# Revit family: QF_ELECTROLUXPROFESSIONAL_1LSN0H_TD6-7_E
name_source: partatom
category: Attrezzature speciali
units: mm (PartAtom-declared; Revit-internal decimal feet)

## family parameters
Basato su piano di lavoro = No
Condiviso = No
Punto di calcolo locali = No
Quota connettore circolare = Usa diametro
Sempre verticale = Sì
Taglio con vuoti quando caricato = No
Tipo di parte = Normale

## types (74) — shared parameters
Depth Actual = 845 mm  [stored 2.77231 ft]
Height Actual = 1050 mm
Latent Heat Output = 0.0
Length Actual = 600 mm  [stored 1.9685 ft]
Modello = TD6-7
Produttore = Electrolux Professional
Sensible Heat Output = 0.0
URL = www.electroluxprofessional.com
Weight = 109
zero-valued in all types: Gas KW, Prospetto di default, Steam Pounds per Hour

## per-type parameters (varying)
| type | Cycle | Descrizione | Item Number | Phase | Volts | Watts |
| 9871830026 | 60 Hz | TUMBLE DRYER TD6-7 MARINE 7KG GALVA.DRUM EL 6KW 230/60/3 COMPASS PRO 6G82 SE SILVER DO.LEFT DISCON. | 1L0EHY | 3 | 230 V | 6300 W |
| 9871830016 | 50 Hz | TUMBLE DRYER TD6-7 7KG SST DRUM EL 6KW 400/50/3N COMPASS PRO 6L80 EU SILVER DO.LEFT EXT.PM. DISCON. 2.I/O | 1L0EGP | 3 | 400 V | 6300 W |
| 9871830160 | 60 Hz | TUMBLE DRYER TD6-7 7KG SST DRUM EL 6KW 200/60/3 COMPASS PRO 6G86 JP SILVER DO.LEFT DISCON. | 1L0H7K | 3 | 200 V | 6300 W |
| 9871830140 | 60 Hz | TUMBLE DRYER TD6-7 7KG GALVA.DRUM EL 6KW 208-240/60/3 COMPASS PRO 6G81 EU SILVER DO.LEFT.INS. MB DISCON. | 1LA244 | 3 | 240 V | 4800 W |
| 9871830056 | 50 Hz | TUMBLE DRYER TD6-7 MARINE 7KG GALVA.DRUM EL 3KW 220-230/50/1N COMPASS PRO 6G81 SE SILVER DO.LEFT MB DISCON. | 1LSN72 | 1 | 230 V | 3300 W |
| 9871830031 | 50 Hz | TUMBLE DRYER TD6-7 7KG GALVA.DRUM EL 6KW 400/50/3N COMPASS PRO 6G82 SE SILVER DO.LEFT | 1L0EKF | 3 | 400 V | 6300 W |
| 9871830096 | 50 Hz | TUMBLE DRYER TD6-7 MARINE 7KG GALVA.DRUM EL 6KW 230/50/3 COMPASS PRO 6G81 SE SILVER DO.LEFT MB DISCON. | 1L0EPL | 3 | 230 V | 6300 W |
| 9871830086 | 60 Hz | TUMBLE DRYER TD6-7 MARINE 7KG GALVA.DRUM EL 4,5KW 230/60/1 COMPASS PRO 6G82 EU SILVER DO.LEFT DISCON. | 1L0ENK | 1 | 230 V | 3300 W |
| 9871830001 | 50 Hz | TUMBLE DRYER TD6-7 7KG SST DRUM EL 6KW 400/50/3N COMPASS PRO 6A81 SE SILVER DO.LEFT.INS. MB | 1LSN1V | 3 | 400 V | 6300 W |
| 9871830011 | 50 Hz | TUMBLE DRYER TD6-7 7KG SST DRUM EL 6KW 230/50/1N COMPASS PRO 6G81 EU SILVER DO.LEFT.INS. MB DISCON. | 1LSN23 | 1 | 230 V | 3300 W |
| 9871830061 | 60 Hz | TUMBLE DRYER TD6-7 7KG GALVA.DRUM EL 4,5KW 208-240/60/1 COMPASS PRO 6L80 EU SILVER DO.LEFT DISCON. | 1L0EKU | 1 | 240 V | 3300 W |
| 9871830051 | 50 Hz | TUMBLE DRYER TD6-7 7KG GALVA.DRUM EL 6KW 400/50/3N COMPASS PRO 6G81 EU SILVER DO.LEFT.INS. ELS-NETW. PREP.CB MB DISCON. | 1L8213 | 3 | 400 V | 6300 W |
| 9871830168 | 60 Hz | TUMBLE DRYER TD6-7 MARINE 7KG SST DRUM EL 6KW 400/60/3N COMPASS PRO 6G81 EU SST/SILVER DO.LEFT PREP.CB MB DISCON. 2.I/O | 1LM0CB | 3 | 400 V | 6300 W |
| 9871830039 | 50 Hz | TUMBLE DRYER TD6-7 7KG SST DRUM EL 6KW 400/50/3N COMPASS PRO 6L80 EU SST/SILVER DO.LEFT EXT.PM. DISCON. 2.I/O | 1L80HG | 3 | 400 V | 6300 W |
| 9871830029 | 50 Hz | TUMBLE DRYER TD6-7 7KG SST DRUM EL 3KW 220-230/50/1N COMPASS PRO 6L80 EU SST/SILVER DO.LEFT EXT.PM. DISCON. 2.I/O | 1L0EJZ | 1 | 230 V | 3300 W |
| 9871830019 | 60 Hz | TUMBLE DRYER TD6-7 MARINE 7KG SST DRUM EL 3KW 230/60/1N COMPASS PRO 6G81 EU SILVER DO.LEFT MB DISCON. | 1L0EGT | 1 | 230 V | 3300 W |
| 9871830105 | 50 Hz | TUMBLE DRYER TD6-7 MARINE 7KG GALVA.DRUM EL 4,5KW 400/50/3 COMPASS PRO 6G81 SE SILVER DO.LEFT MB DISCON. | 1L0FUW | 3 | 400 V | 4800 W |
| 9871830079 | 60 Hz | TUMBLE DRYER TD6-7 MARINE 7KG GALVA.DRUM EL 6KW 400/60/3N COMPASS PRO 6G81 SE SILVER DO.LEFT MB DISCON. | 1L0ELT | 3 | 400 V | 6300 W |
| 9871830059 | 50 Hz | TUMBLE DRYER TD6-7 7KG GALVA.DRUM EL 6KW 400/50/3N COMPASS PRO 6G81 EU SILVER DO.LEFT MB DISCON. | 1L0EKK | 3 | 400 V | 6300 W |
| 9871830115 | 60 Hz | TUMBLE DRYER TD6-7 7KG GALVA.DRUM EL 6KW 400/60/3N COMPASS PRO 6G81 EU SILVER DO.LEFT MB DISCON. | 1LSNUM | 3 | 400 V | 6300 W |
| 9871830125 | 50 Hz | TUMBLE DRYER TD6-7 7KG SST DRUM EL 3KW 240/50/1N COMPASS PRO 6G81 EU SILVER DO.LEFT MB DISCON. | 1LSP7Z | 1 | 240 V | 3300 W |
| 9871830034 | 50 Hz | TUMBLE DRYER TD6-7 7KG GALVA.DRUM EL 3KW 240/50/1N COMPASS PRO 6G82 EU SILVER DO.LEFT DISCON. | 1L80HR | 1 | 240 V | 3300 W |
| 9871830014 | 50 Hz | TUMBLE DRYER TD6-7 7KG SST DRUM EL 6KW 230/50/1N COMPASS PRO 6G81 EU SILVER DO.LEFT MB DISCON. | 1L0EGM | 1 | 230 V | 6300 W |
| 9871830089 | 60 Hz | TUMBLE DRYER TD6-7 MARINE 7KG GALVA.DRUM EL 6KW 480/60/3 COMPASS PRO 6G81 SE SILVER DO.LEFT MB DISCON. | 1LSNDV | 3 | 480 V | 6300 W |
| 9871830064 | 60 Hz | TUMBLE DRYER TD6-7 MARINE 7KG SST DRUM EL 3KW 230/60/1 COMPASS PRO 6G81 EU SILVER DO.LEFT MB DISCON. | 1LSN83 | 1 | 230 V | 3300 W |
| 9871830044 | 50 Hz | TUMBLE DRYER TD6-7 7KG SST DRUM EL 6KW 415/50/3 COMPASS PRO 6G81 EU SILVER DO.LEFT MB DISCON. | 1LSN4P | 3 | 415 V | 6300 W |
| 9871830084 | 50 Hz | TUMBLE DRYER TD6-7 7KG GALVA.DRUM EL 6KW 400/50/3N COMPASS PRO 6G81 EU SILVER DO.LEFT PREP.CB MB DISCON. 2.I/O | 1LSNB2 | 3 | 400 V | 6300 W |
| 9871830126 | 50 Hz | TUMBLE DRYER TD6-7 7KG SST DRUM EL 6KW 400/50/3N COMPASS PRO 6G81 EU SILVER DO.LEFT MB DISCON. | 1L0GAN | 3 | 400 V | 6300 W |
| 9871830116 | 60 Hz | TUMBLE DRYER TD6-7 7KG GALVA.DRUM EL 6KW 400/60/3N COMPASS PRO 6G82 EU SILVER DO.LEFT DISCON. | 1LSNUN | 3 | 400 V | 6300 W |
| 9871830106 | 60 Hz | TUMBLE DRYER TD6-7 MARINE 7KG SST DRUM EL 3KW 208-240/60/1 COMPASS PRO 6L80 EU SILVER DO.LEFT EXT.PM. DISCON. 2.I/O | 1LSNHX | 1 | 240 V | 3300 W |
| 9871830176 | 50 Hz | TUMBLE DRYER TD6-7 7KG SST DRUM EL 6KW 400/50/3N COMPASS PRO 6G82 EU SILVER DO.LEFT.INS. DISCON. | 1LT6US | 3 | 400 V | 6300 W |
| 9871830173 | 50 Hz | TUMBLE DRYER TD6-7 MARINE 7KG GALVA.DRUM EL 4,5KW 230/50/1 COMPASS PRO 6G81 EU SILVER DO.LEFT MB DISCON. | 1LT6UD | 1 | 230 V | 4800 W |
| 9871830067 | 50 Hz | TUMBLE DRYER TD6-7 MARINE 7KG SST DRUM EL 6KW 400/50/3 COMPASS PRO 6G81 EU SILVER DO.LEFT MB DISCON. | 1L0ELR | 3 | 400 V | 4800 W |
| 9871830057 | 50 Hz | TUMBLE DRYER TD6-7 MARINE 7KG GALVA.DRUM EL 6KW 400/50/3 COMPASS PRO 6G81 SE SILVER DO.LEFT MB DISCON. | 1LSN73 | 3 | 400 V | 4800 W |
| 9871830047 | 60 Hz | TUMBLE DRYER TD6-7 MARINE 7KG GALVA.DRUM EL 6KW 440/60/3 COMPASS PRO 6G82 EU SST/SILVER DO.LEFT DISCON. | 1L0EKH | 3 | 440 V | 6300 W |
| 9871830153 | 60 Hz | TUMBLE DRYER TD6-7 MARINE 7KG SST DRUM EL 4,5KW 400/60/3N COMPASS PRO 6G81 SE SST/SILVER DO.LEFT MB DISCON. | 1LSPRS | 3 | 400 V | 4800 W |
| 9871830032 | 50 Hz | TUMBLE DRYER TD6-7 7KG GALVA.DRUM EL 6KW 400/50/3N COMPASS PRO 6L80 EU SILVER DO.LEFT EXT.PM. DISCON. 2.I/O | 1L80HE | 3 | 400 V | 6300 W |
| 9871830097 | 50 Hz | TUMBLE DRYER TD6-7 7KG GALVA.DRUM EL 3KW 240/50/1N COMPASS PRO 6G82 EU SILVER DO.LEFT ELS-NETW. DISCON. | 1L0ERE | 1 | 240 V | 3300 W |
| 9871830012 | 60 Hz | TUMBLE DRYER TD6-7 MARINE 7KG SST DRUM EL 6KW 440/60/3 COMPASS PRO 6G81 EU SILVER DO.LEFT.INS. MB DISCON. | 1LSN24 | 3 | 440 V | 6300 W |
| 9871830002 | 50 Hz | TUMBLE DRYER TD6-7 7KG SST DRUM EL 6KW 400/50/3N COMPASS PRO 6G81 EU SILVER DO.LEFT MB DISCON. | 1LSN0E | 3 | 400 V | 6300 W |
| 9871830087 | 60 Hz | TUMBLE DRYER TD6-7 MARINE 7KG SST DRUM EL 6KW 400/60/3N COMPASS PRO 6G81 EU SST/SILVER DO.LEFT MB DISCON. | 1LSNCS | 3 | 400 V | 6300 W |
| 9871830062 | 60 Hz | TUMBLE DRYER TD6-7 7KG GALVA.DRUM EL 4,5KW 208-240/60/3 COMPASS PRO 6L80 EU SILVER DO.LEFT DISCON. | 1L0EKV | 3 | 240 V | 4800 W |
| 9871830082 | 50 Hz | TUMBLE DRYER TD6-7 7KG SST DRUM EL 6KW 240/50/1N COMPASS PRO 6G81 EU SILVER DO.LEFT MB DISCON. | 1L0ENC | 1 | 240 V | 3300 W |
| 9871830114 | 50 Hz | TUMBLE DRYER TD6-7 7KG GALVA.DRUM EL 3KW 230/50/1N COMPASS PRO 6G82 EU SILVER DO.LEFT DISCON. | 1LSNPP | 1 | 230 V | 3300 W |
| 9871830131 | 60 Hz | TUMBLE DRYER TD6-7 MARINE 7KG GALVA.DRUM EL 6KW 400/60/3N COMPASS PRO 6L80 EU SILVER DO.LEFT EXT.PM. DISCON. 2.I/O | 1L0GEE | 3 | 400 V | 6300 W |
| 9871830035 | 60 Hz | TUMBLE DRYER TD6-7 MARINE 7KG GALVA.DRUM EL 6KW 440/60/3 COMPASS PRO 6G82 EU SILVER DO.LEFT DISCON. | 1L80HS | 3 | 440 V | 6300 W |
| 9871830111 | 60 Hz | TUMBLE DRYER TD6-7 MARINE 7KG SST DRUM EL 6KW 230/60/3 COMPASS PRO 6G81 EU SILVER DO.LEFT MB DISCON. | 1L0FYC | 3 | 230 V | 6300 W |
| 9871830015 | 60 Hz | TUMBLE DRYER TD6-7 MARINE 7KG SST DRUM EL 6KW 440/60/3 COMPASS PRO 6G81 EU SILVER DO.LEFT MB DISCON. | 1L0EGN | 3 | 440 V | 6300 W |
| 9871830121 | 50 Hz | TUMBLE DRYER TD6-7 7KG SST DRUM EL 6KW 230/50/1N COMPASS PRO 6L80 EU SILVER DO.LEFT EXT.PM. DISCON. 2.I/O | 1LA19F | 1 | 230 V | 3300 W |
| 9871830005 | 50 Hz | TUMBLE DRYER TD6-7 7KG SST DRUM EL 6KW 400/50/3N COMPASS PRO 6L80 EU SILVER DO.LEFT.INS. EXT.PM. DISCON. 2.I/O | 1LSN1Y | 3 | 400 V | 6300 W |
| 9871830065 | 60 Hz | TUMBLE DRYER TD6-7 MARINE 7KG GALVA.DRUM EL 6KW 400/60/3 COMPASS PRO 6G81 SE SILVER DO.LEFT MB DISCON. | 1LSN8F | 3 | 400 V | 6300 W |
| 9871830045 | 50 Hz | TUMBLE DRYER TD6-7 MARINE 7KG GALVA.DRUM EL 6KW 400/50/3 COMPASS PRO 6G82 EU SILVER DO.LEFT DISCON. | 1LSN4R | 3 | 400 V | 4800 W |
| 9871830030 | 50 Hz | TUMBLE DRYER TD6-7 7KG SST DRUM EL 3KW 220-230/50/1N COMPASS PRO 6L80 EU SILVER DO.LEFT EXT.PM. DISCON. 2.I/O | 1L0EK0 | 1 | 230 V | 3300 W |
| 9871830095 | 50 Hz | TUMBLE DRYER TD6-7 7KG SST DRUM EL 6KW 400/50/3 COMPASS PRO 6G81 EU SST/SILVER DO.LEFT MB DISCON. | 1L0EP5 | 3 | 400 V | 4800 W |
| 9871830129 | 50 Hz | TUMBLE DRYER TD6-7 7KG SST DRUM EL 4,5KW 220-230/50/1N COMPASS PRO 6G81 EU SILVER DO.LEFT MB DISCON. | 1L0GB8 | 1 | 230 V | 4800 W |
| 9871830139 | 50 Hz | TUMBLE DRYER TD6-7 7KG SST DRUM EL 6KW 230/50/3 COMPASS PRO 6L80 EU SILVER DO.LEFT.INS. EXT.PM. DISCON. 2.I/O | 1L0GTP | 3 | 230 V | 6300 W |
| 9871830085 | 60 Hz | TUMBLE DRYER TD6-7 7KG GALVA.DRUM EL 6KW 230/60/3 COMPASS PRO 6G82 EU SILVER DO.LEFT DISCON. | 1LSNBF | 3 | 230 V | 6300 W |
| 9871830060 | 50 Hz | TUMBLE DRYER TD6-7 7KG GALVA.DRUM EL 6KW 415/50/3N COMPASS PRO 6L80 EU SILVER DO.LEFT PREP.CB DISCON. 2.I/O | 1L821A | 3 | 415 V | 6300 W |
| 9871830159 | 50 Hz | TUMBLE DRYER TD6-7 7KG SST DRUM EL 6KW 200/50/3 COMPASS PRO 6G86 JP SILVER DO.LEFT DISCON. | 1L0H7J | 3 | 200 V | 6300 W |
| 9871830040 | 60 Hz | TUMBLE DRYER TD6-7 MARINE 7KG GALVA.DRUM EL 6KW 440/60/3 COMPASS PRO 6G82 EU SILVER DO.LEFT DISCON. | 1L80HY | 3 | 440 V | 6300 W |
| 9871830119 | 50 Hz | TUMBLE DRYER TD6-7 7KG GALVA.DRUM EL 3KW 220-230/50/1N COMPASS PRO 6G81 EU SILVER DO.LEFT MB DISCON. | 1LSNXJ | 1 | 230 V | 3300 W |
| 9871830038 | 50 Hz | TUMBLE DRYER TD6-7 7KG GALVA.DRUM EL 6KW 230/50/3 COMPASS PRO 6G81 EU SILVER DO.LEFT MB DISCON. | 1L80H4 | 3 | 230 V | 6300 W |
| 9871830102 | 60 Hz | TUMBLE DRYER TD6-7 7KG SST DRUM EL 6KW 400/60/3N COMPASS PRO 6G81 EU SST/SILVER DO.LEFT.INS. MB DISCON. | 1LSNGU | 3 | 400 V | 6300 W |
| 9871830068 | 60 Hz | TUMBLE DRYER TD6-7 7KG SST DRUM EL 6KW 440/60/3 COMPASS PRO 6G81 EU SILVER DO.LEFT MB DISCON. | 1L0EML | 3 | 440 V | 6300 W |
| 9871830048 | 60 Hz | TUMBLE DRYER TD6-7 MARINE 7KG GALVA.DRUM EL 6KW 440/60/3 COMPASS PRO 6L80 EU SST/SILVER DO.LEFT EXT.PM. DISCON. 2.I/O | 1L0EKJ | 3 | 440 V | 6300 W |
| 9871830142 | 50 Hz | TUMBLE DRYER TD6-7 7KG GALVA.DRUM EL 6KW 400/50/3N COMPASS PRO 6G82 EU SST/SILVER DO.LEFT DISCON. | 1LA24L | 3 | 400 V | 6300 W |
| 9871830033 | 50 Hz | TUMBLE DRYER TD6-7 7KG GALVA.DRUM EL 6KW 400/50/3N COMPASS PRO 6G82 EU SILVER DO.LEFT DISCON. | 1L80HF | 3 | 400 V | 6300 W |
| 9871830023 | 60 Hz | TUMBLE DRYER TD6-7 MARINE 7KG SST DRUM EL 6KW 400/60/3 COMPASS PRO 6G81 EU SILVER DO.LEFT MB DISCON. | 1L0EJ2 | 3 | 400 V | 6300 W |
| 9871830013 | 50 Hz | TUMBLE DRYER TD6-7 7KG SST DRUM EL 6KW 400/50/3N COMPASS PRO 6A81 SE SILVER DO.LEFT MB | 1L0EGL | 3 | 400 V | 63000 W |
| 9871830088 | 60 Hz | TUMBLE DRYER TD6-7 MARINE 7KG SST DRUM EL 6KW 400/60/3N COMPASS PRO 6L80 EU SST/SILVER DO.LEFT EXT.PM. DISCON. 2.I/O | 1LSNCT | 3 | 400 V | 6300 W |
| 9871830137 | 50 Hz | TUMBLE DRYER TD6-7 7KG SST DRUM EL 6KW 400/50/3N COMPASS PRO 6G81 EU SST DO.LEFT MB DISCON. | 1LSPE0 | 3 | 400 V | 6300 W |
| 9871830107 | 60 Hz | TUMBLE DRYER TD6-7 7KG SST DRUM EL 6KW 230/60/3 COMPASS PRO 6G81 EU SILVER DO.LEFT MB DISCON. | 1L0FVC | 3 | 230 V | 6300 W |
| 9871830130 | 50 Hz | TUMBLE DRYER TD6-7 7KG SST DRUM EL 3KW 220-230/50/1N COMPASS PRO 6G82 EU SILVER DO.LEFT DISCON. | 1LSPAV | 1 | 230 V | 3300 W |
| 9871830120 | 60 Hz | TUMBLE DRYER TD6-7 7KG GALVA.DRUM EL 3KW 240/60/1 COMPASS PRO 6G82 EU SILVER DO.LEFT DISCON. | 1LA1BF | 1 | 240 V | 3300 W |

note: [stored X ft] marks values corroborated as IEEE doubles in the binary element streams (Revit-internal decimal feet)

## geometry (parser evidence)
native form markers: Blend x12
no freeform markers — native parametric forms only
